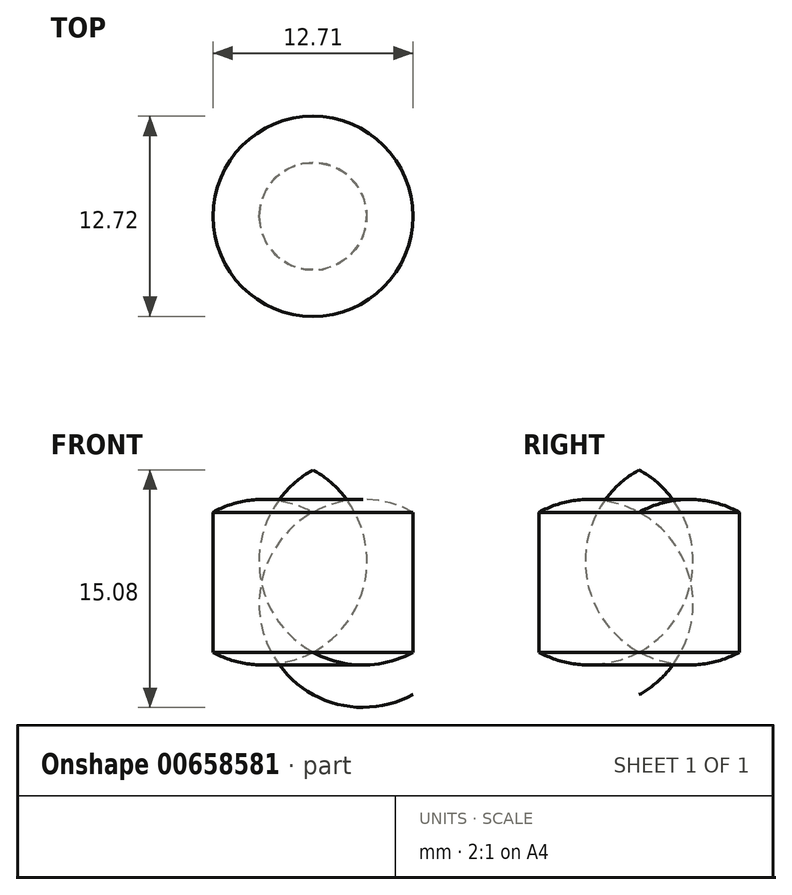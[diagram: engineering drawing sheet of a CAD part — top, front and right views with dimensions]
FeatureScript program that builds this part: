
annotation { "Feature Type Name" : "Feature", "Feature Type Description" : "" }
export const myFeature = defineFeature(function(context is Context, id is Id, definition is map)
    precondition{}
    {
        {
            var Q0;
            Q0=qCreatedBy(makeId("Front.planeOp"),FACE);
            var sketch = newSketch(context, id + "F0", { "sketchPlane" : qUnion([Q0])});
            skLineSegment(sketch, "E0", {"start": v(-6.36, -0.33) * mm, "end": v(-6.36, -9.22) * mm});
            skArc(sketch, "E1", {"start": v(0, -0.33) * mm, "mid": v(-3.18, 0.49) * mm, "end": v(-6.36, -0.33) * mm});
            skArc(sketch, "E2", {"start": v(-6.36, -9.22) * mm, "mid": v(-3.18, -10.03) * mm, "end": v(0, -9.22) * mm});
            skLineSegment(sketch, "E3", {"start": v(0, -0.33) * mm, "end": v(0, -9.22) * mm});
            skSolve(sketch);
        }
        {
            var Q0;
            Q0=makeQuery(id+"F0.imprint","IMPRINT",FACE,{"disambiguationData":[TD([[makeQuery(id+"F0.imprint","IMPRINT",EDGE,{"derivedFrom":sQuery(id+"F0.wireOp",EDGE,"E0")}),1.0]])]});
            var Q1;
            Q1=sQuery(id+"F0.wireOp",EDGE,"E0");
            revolve(context, id + "F1", {"entities" : qUnion([Q0]), "axis" : qUnion([Q1]), "revolveType" : RevolveType.FULL});
        }
    });
